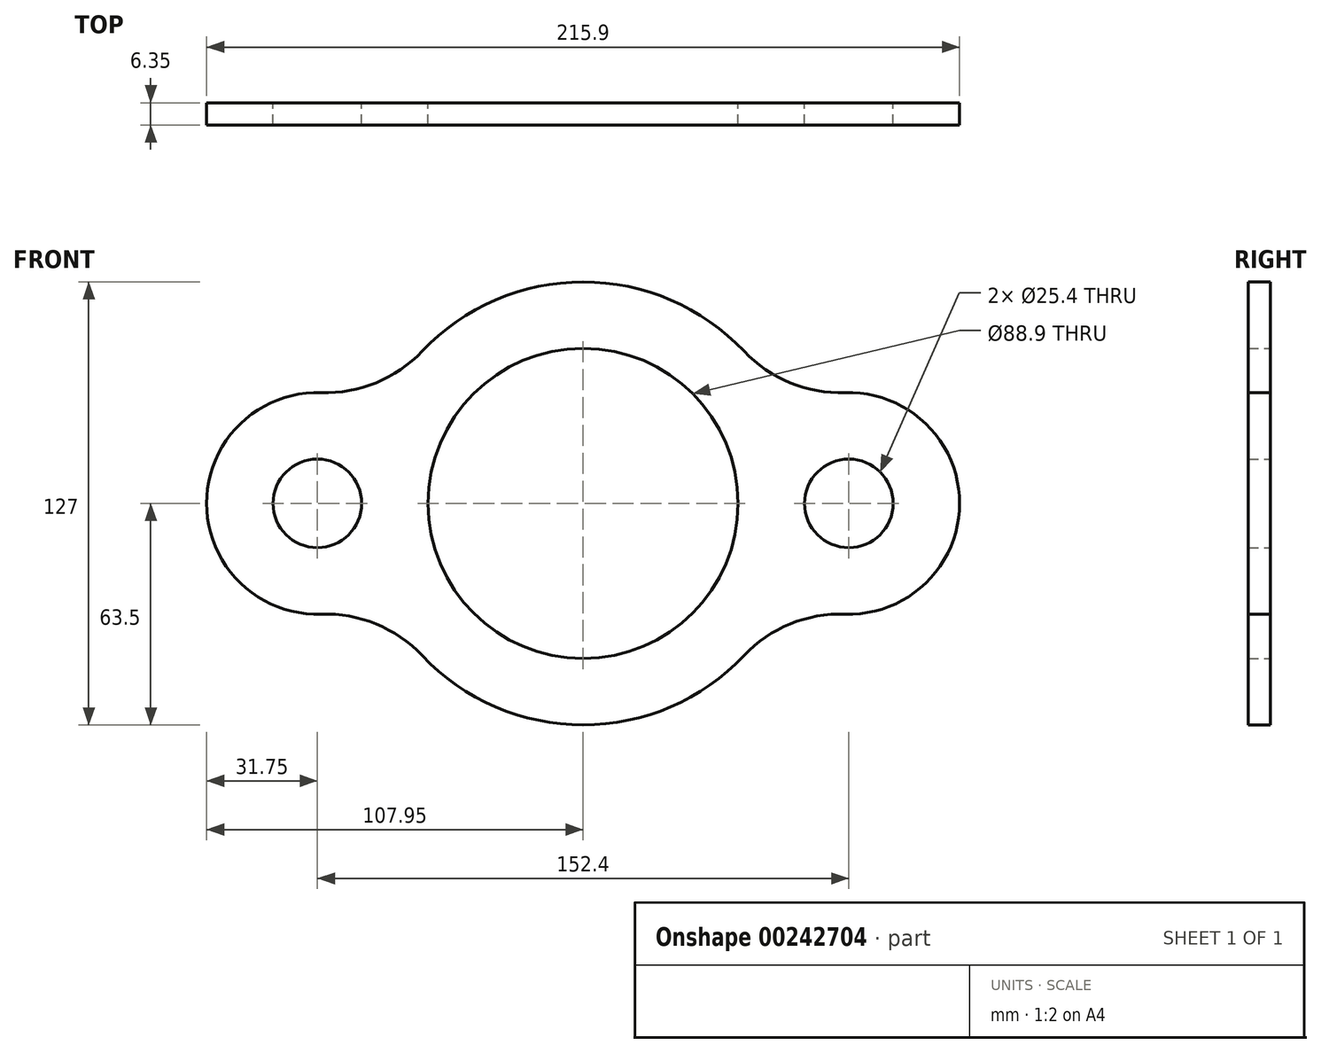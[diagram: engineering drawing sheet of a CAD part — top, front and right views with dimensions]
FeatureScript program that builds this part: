
annotation { "Feature Type Name" : "Feature", "Feature Type Description" : "" }
export const myFeature = defineFeature(function(context is Context, id is Id, definition is map)
    precondition{}
    {
        {
            var Q0;
            Q0=qCreatedBy(makeId("Front.planeOp"),FACE);
            var sketch = newSketch(context, id + "F0", { "sketchPlane" : qUnion([Q0])});
            skArc(sketch, "E0", {"start": v(-46.14, -43.63) * mm, "mid": v(0, -63.5) * mm, "end": v(46.14, -43.63) * mm});
            skCircle(sketch, "E1", {"center": v(0, 0) * mm, "radius": 44.45 * mm});
            skArc(sketch, "E2", {"start": v(-75.12, 31.73) * mm, "mid": v(-107.95, 0) * mm, "end": v(-75.12, -31.73) * mm});
            skArc(sketch, "E3", {"start": v(75.12, -31.73) * mm, "mid": v(107.95, 0) * mm, "end": v(75.12, 31.73) * mm});
            skCircle(sketch, "E4", {"center": v(-76.2, 0) * mm, "radius": 12.7 * mm});
            skCircle(sketch, "E5", {"center": v(76.2, 0) * mm, "radius": 12.7 * mm});
            skArc(sketch, "E6.trimOffspring", {"start": v(46.14, 43.63) * mm, "mid": v(0, 63.5) * mm, "end": v(-46.14, 43.63) * mm});
            skArc(sketch, "E7.filletArc", {"start": v(-75.12, 31.73) * mm, "mid": v(-59.35, 34.56) * mm, "end": v(-46.14, 43.63) * mm});
            skArc(sketch, "E8.filletArc", {"start": v(46.14, 43.63) * mm, "mid": v(59.35, 34.56) * mm, "end": v(75.12, 31.73) * mm});
            skArc(sketch, "E9.filletArc", {"start": v(-46.14, -43.63) * mm, "mid": v(-59.35, -34.56) * mm, "end": v(-75.12, -31.73) * mm});
            skArc(sketch, "E10.filletArc", {"start": v(75.12, -31.73) * mm, "mid": v(59.35, -34.56) * mm, "end": v(46.14, -43.63) * mm});
            skSolve(sketch);
        }
        {
            var Q0;
            Q0 = qSketchRegion(id + "F0", true);
            extrude(context, id + "F1", {"entities" : qUnion([Q0]), "depth" : 6.35 * mm});
        }
    });
